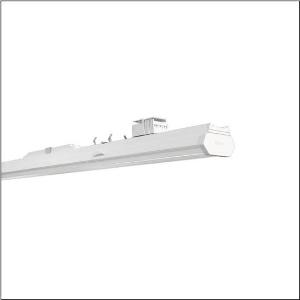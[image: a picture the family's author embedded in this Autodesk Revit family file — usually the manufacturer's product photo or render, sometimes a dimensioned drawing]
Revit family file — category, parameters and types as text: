
# Revit family: licross_r__11_protected_mo_51tp12dn495g3s4_346c
name_source: partatom
category: Lighting Fixtures
units: mm (PartAtom-declared; Revit-internal decimal feet)

## family parameters
Cut with Voids When Loaded = No
Host = Face
Light Source = No
Part Type = Normal
Room Calculation Point = No
Round Connector Dimension = Use Diameter
Shared = No

## types (1)
- --- (1 x LED, 980 lm, 6.8 W, 4000K)
    Apparent Load = 7 VA
    CIE Flux Codes = 73 92 98 99 100
    Color Rendering = 80
    Color Temperature = 4000K
    Default Elevation = 1800 mm
    Description = Licross® 11 Protected MO, luminaire insert, of sheet steel, galvanised, coil coated, white, length: 1.500mm, width: 90mm, height: 101mm, LED rated luminous flux: 9.980lm, light colour: 840, control gear: DALI 2, with plug, 6-pole, with phase selection, for trunking rail, 9 or 11-core, mains connection: 220..240V, AC, 50/60Hz, rated input power: 61W, for trunking rail, 9-/11-core, halogen-free wiring, for emergency light function, converter,control gear: single battery element, battery: LiFePO4, 9Ah, primary light control with lens, of plastic, primary optical cover: cover, of PMMA, light emission: direct distribution, primary light characteristic: symmetric, protection rating (complete): IP64, insulation class (complete): insulation class I (protective earthing), certification: CE, UKCA, protection symbol: D if used in an environment with conductive dust loads with corresponding accessories, impact resistance: IK06, permissible ambient temperature for indoor applications: +5..+35°C, standard: EN 60598-2-22, LABS conformity tested according to VDMA 24364:2018-05, reducing of maximum allowable ambient temperature of 5°C with ceiling mounting, corresponds to IFS (International Featured Standards) requirements for safety and quality in the food industry, packaging unit: 1 piece
    Height = 92 mm
    Lamp = 1 x LED
    Lamp Light Flux = 980 lm
    Lamp Power = 6.8 W
    Lamp count = 1
    Length = 1500 mm
    Luminous efficacy = 144 lm/W
    Manufacturer = Siteco
    ModVariant = No
    Model = 51TP12DN495G3S4
    Mounting Place = Ceiling
    Mounting Type = Pendant
    Number of Poles = 1
    OnlyDefault = Yes
    Power Factor = 1
    Product Name = Licross® 11 Protected MO
    Product group = luminaire insert
    ProductGroupID = 901
    Protection Class = Protection class I
    Protection Degree = IP 64
    RLX_Detail_Level = 1
    RLX_Emergency_Light_Flux = 0 lm
    RLX_Emergency_Type = 0
    RLX_Emergency_Type_DB = No
    RlxData = <blob elided: 24817 chars, md5=9c70925a>
    Socket = socket
    Standby Power = 0 W
    System Light Flux = 980 lm
    System Power = 7 W
    Type Comments = : emergency light operation: 3 h
    Type Image = l_1256148.jpg
    URL = http://relux.com
    VarID = @adj_059355
    Voltage = 0 V
    Weight = 0.00 kg
    Width = 88 mm

## geometry (parser evidence)
native form markers: Blend x4, Sweep x12
no freeform markers — native parametric forms only
